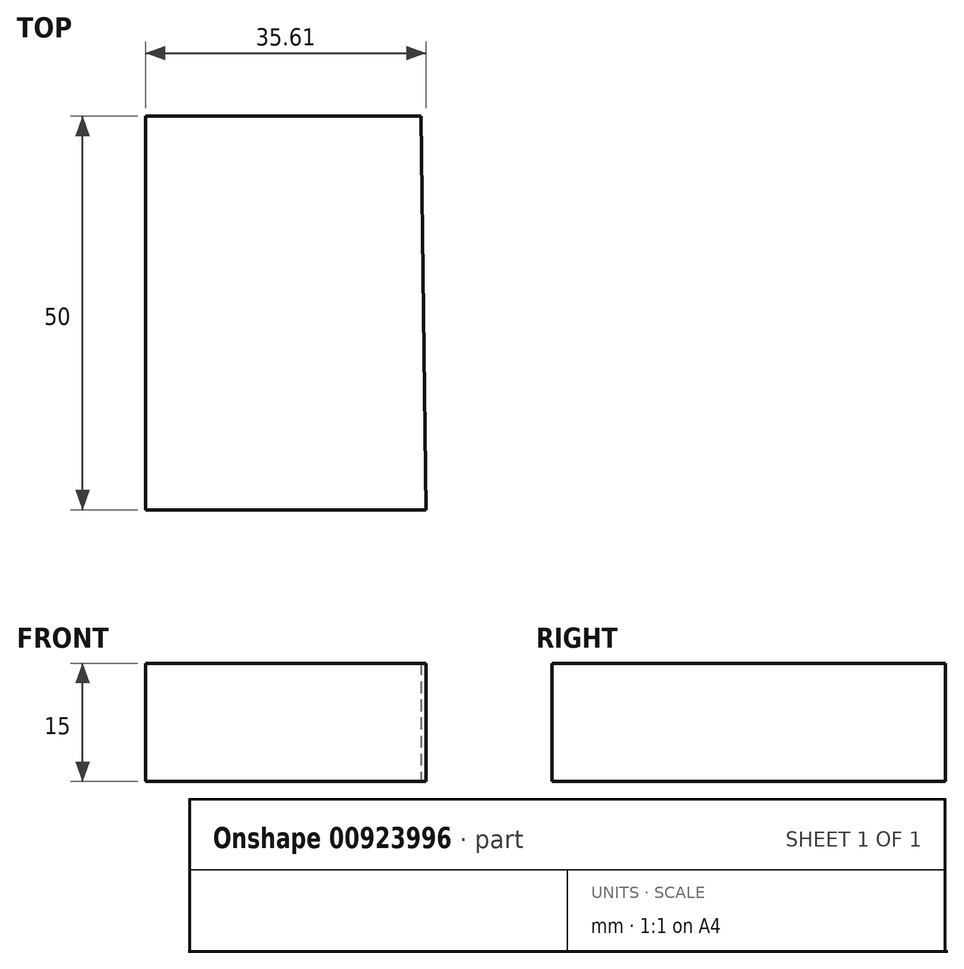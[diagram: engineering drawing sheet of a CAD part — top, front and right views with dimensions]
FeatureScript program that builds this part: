
annotation { "Feature Type Name" : "Feature", "Feature Type Description" : "" }
export const myFeature = defineFeature(function(context is Context, id is Id, definition is map)
    precondition{}
    {
        {
            var Q0;
            Q0=qCreatedBy(makeId("Top.planeOp"),FACE);
            var sketch = newSketch(context, id + "F0", { "sketchPlane" : qUnion([Q0])});
            skLineSegment(sketch, "E0", {"start": v(-11.7, 9) * mm, "end": v(23.3, 9) * mm});
            skLineSegment(sketch, "E1", {"start": v(23.91, -40.99) * mm, "end": v(-11.7, -40.99) * mm});
            skLineSegment(sketch, "E2", {"start": v(-11.7, 9) * mm, "end": v(-11.7, -40.99) * mm});
            skLineSegment(sketch, "E3", {"start": v(23.3, 9) * mm, "end": v(23.91, -40.99) * mm});
            skSolve(sketch);
        }
        {
            var Q0;
            Q0=makeQuery(id+"F0.imprint","IMPRINT",FACE,{"disambiguationData":[TD([[makeQuery(id+"F0.imprint","IMPRINT",EDGE,{"derivedFrom":sQuery(id+"F0.wireOp",EDGE,"E0")}),-1.0]])]});
            extrude(context, id + "F1", {"entities" : qUnion([Q0]), "depth" : 15 * mm, "offsetDistance" : 25 * mm});
        }
    });
